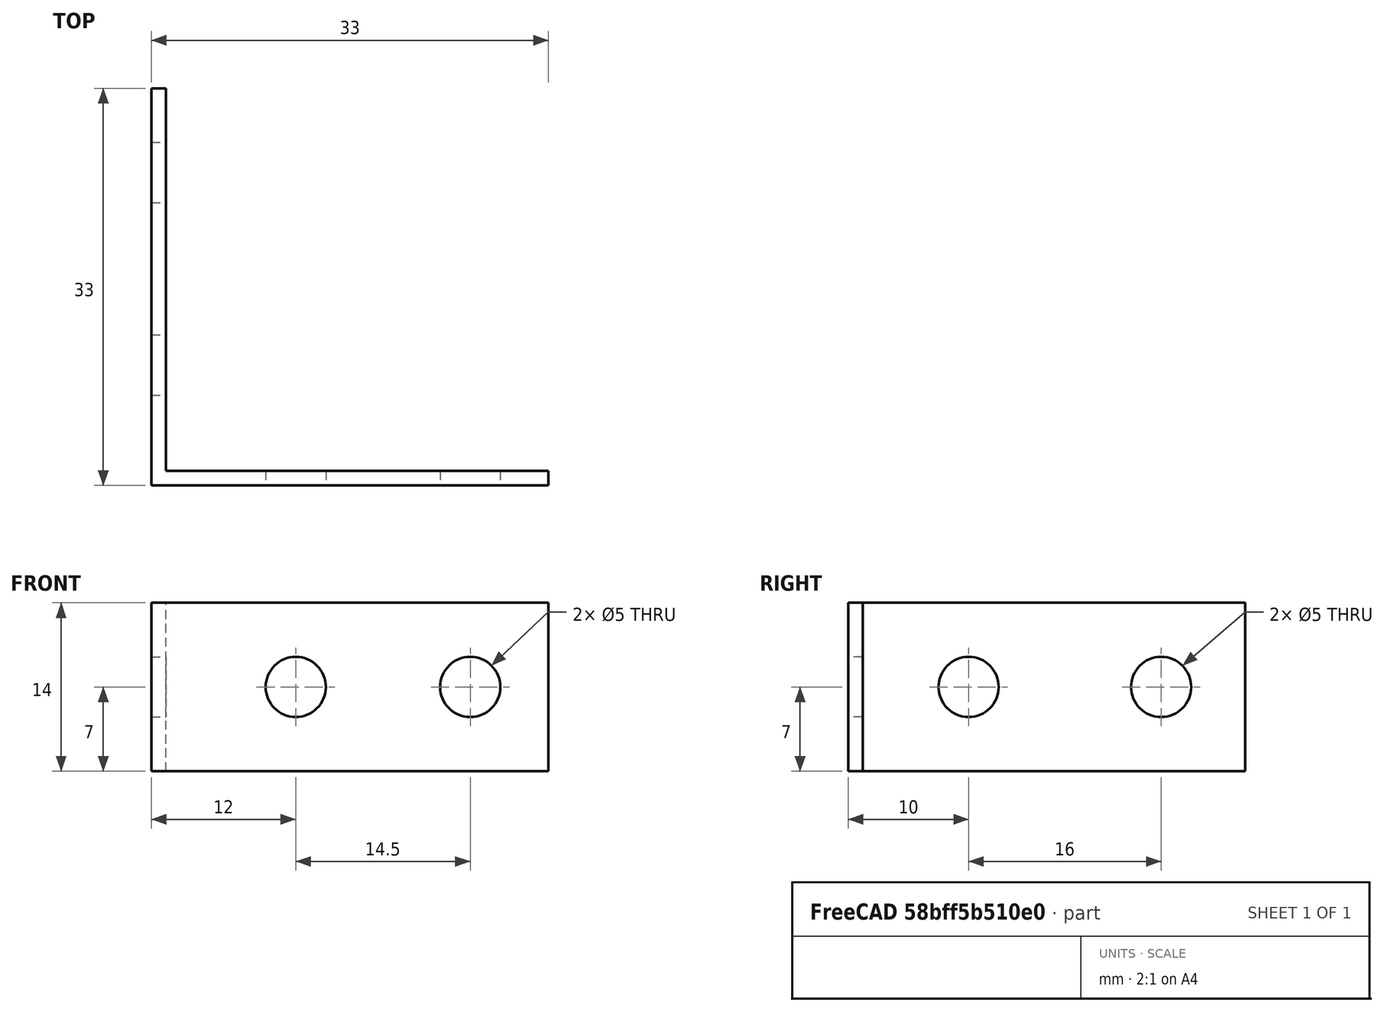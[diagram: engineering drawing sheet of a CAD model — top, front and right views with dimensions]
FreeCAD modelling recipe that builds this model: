
FCSTD DOCUMENT  (FreeCAD 0.17R13541 (Git))
Label: Angulos
License: All rights reserved
LicenseURL: http://en.wikipedia.org/wiki/All_rights_reserved
objects: Part::Cylinder×4, Part::Cut×4, Part::Box×2, Part::MultiFuse×1, Part::Feature×1
note: 12 computed .brp shape members not serialized (recipe doc carries the construction recipe); baked Part::Feature solids carry a one-line shape summary decoded from their .brp

FEATURE [Part::Box] Box001  label="Cubo001"
  AttacherType = Attacher::AttachEngine3D
  Height = 14
  Length = 33
  Width = 1.2
FEATURE [Part::Cylinder] Cylinder  label="Cilindro"
  Angle = 360
  AttacherType = Attacher::AttachEngine3D
  Height = 10
  Placement = pos=(12,7,7) rot=(1,0,0;1.5708rad)
  Radius = 2.5
FEATURE [Part::Cylinder] Cylinder001  label="Cilindro001"
  Angle = 360
  AttacherType = Attacher::AttachEngine3D
  Height = 10
  Placement = pos=(26.5,6,7) rot=(1,0,0;1.5708rad)
  Radius = 2.5
FEATURE [Part::Box] Box002  label="Cubo002"
  AttacherType = Attacher::AttachEngine3D
  Height = 14
  Length = 33
  Width = 1.2
FEATURE [Part::Cut] Cut
  Base = -> Box001
  Refine = true
  Tool = -> Cylinder
FEATURE [Part::Cut] Cut001
  Base = -> Cut
  Refine = true
  Tool = -> Cylinder001
FEATURE [Part::Cylinder] Cylinder002  label="Cilindro002"
  Angle = 360
  AttacherType = Attacher::AttachEngine3D
  Height = 10
  Placement = pos=(10,5,7) rot=(1,0,0;1.5708rad)
  Radius = 2.5
FEATURE [Part::Cylinder] Cylinder003  label="Cilindro003"
  Angle = 360
  AttacherType = Attacher::AttachEngine3D
  Height = 10
  Placement = pos=(26,5,7) rot=(1,0,0;1.5708rad)
  Radius = 2.5
FEATURE [Part::Cut] Cut002
  Base = -> Box002
  Refine = true
  Tool = -> Cylinder002
FEATURE [Part::Cut] Cut003
  Base = -> Cut002
  Placement = pos=(1.2,0,0) rot=(0,0,1;1.5708rad)
  Refine = true
  Tool = -> Cylinder003
FEATURE [Part::MultiFuse] Fusion  label="Angulo-Terminado"
  Refine = true
  Shapes = -> [Cut001,Cut003]
FEATURE [Part::Feature] Fusion001  label="Angulo-Copia"
  shape: bbox 33 x 33 x 14 mm, 12 faces (baked)
